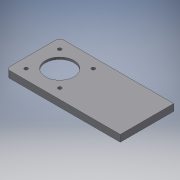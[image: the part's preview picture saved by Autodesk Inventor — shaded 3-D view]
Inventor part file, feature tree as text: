
AUTODESK INVENTOR PART (.ipt)
format: ipt  version: 2018 (Build 220112000, 112)  size: 158,208 bytes
history: native  units: mm
features: other x6, extrude x3, sketch x3, fillet x2
ambient origin geometry x8: Origin, YZ Plane, XZ Plane, XY Plane, X Axis, Y Axis, Z Axis, Center Point
bodies: Body1 (feature_tree)
feature tree (14):
  other  "Sólido1"
  extrude  "Extrusão1"  Depth=160.0mm
  extrude  "Extrusão6"  Depth=9.52mm TaperAngle=0.0deg
  extrude  "Extrusão7"  Depth=59.0mm
  fillet  "Arredondamento1"  Radius=5.0mm
  fillet  "Arredondamento2"  Radius=5.0mm
  sketch  "Esboço1"  dims[d0=160.0mm d1=160.0mm]
  other  "Referência1"
  other  "Referência2"
  sketch  "Esboço9"  dims[d2=75.0mm d3=9.52mm d4=0.0mm]
  sketch  "Esboço10"  dims[d72=59.0mm d73=59.0mm d74=5.0mm d75=5.0mm d76=5.0mm d77=5.0mm d78=23.57mm d79=23.57mm d80=23.57mm d81=23.57mm d82=23.57mm d83=23.57mm d84=23.57mm d85=23.57mm d86=8.0mm d87=8.0mm d88=40.0mm d89=6.52mm d90=0.0mm d91=6.52mm d92=0.0mm d93=6.0mm d94=5.0mm]
  other  "<userpath>\Documents\OpenCNC\MONTAGEM\CNC1.iam"
  other  "CNC1.iam"
  other  "PERFIL_ESTRUTURAL_40X80_EIXO_Y:1"
